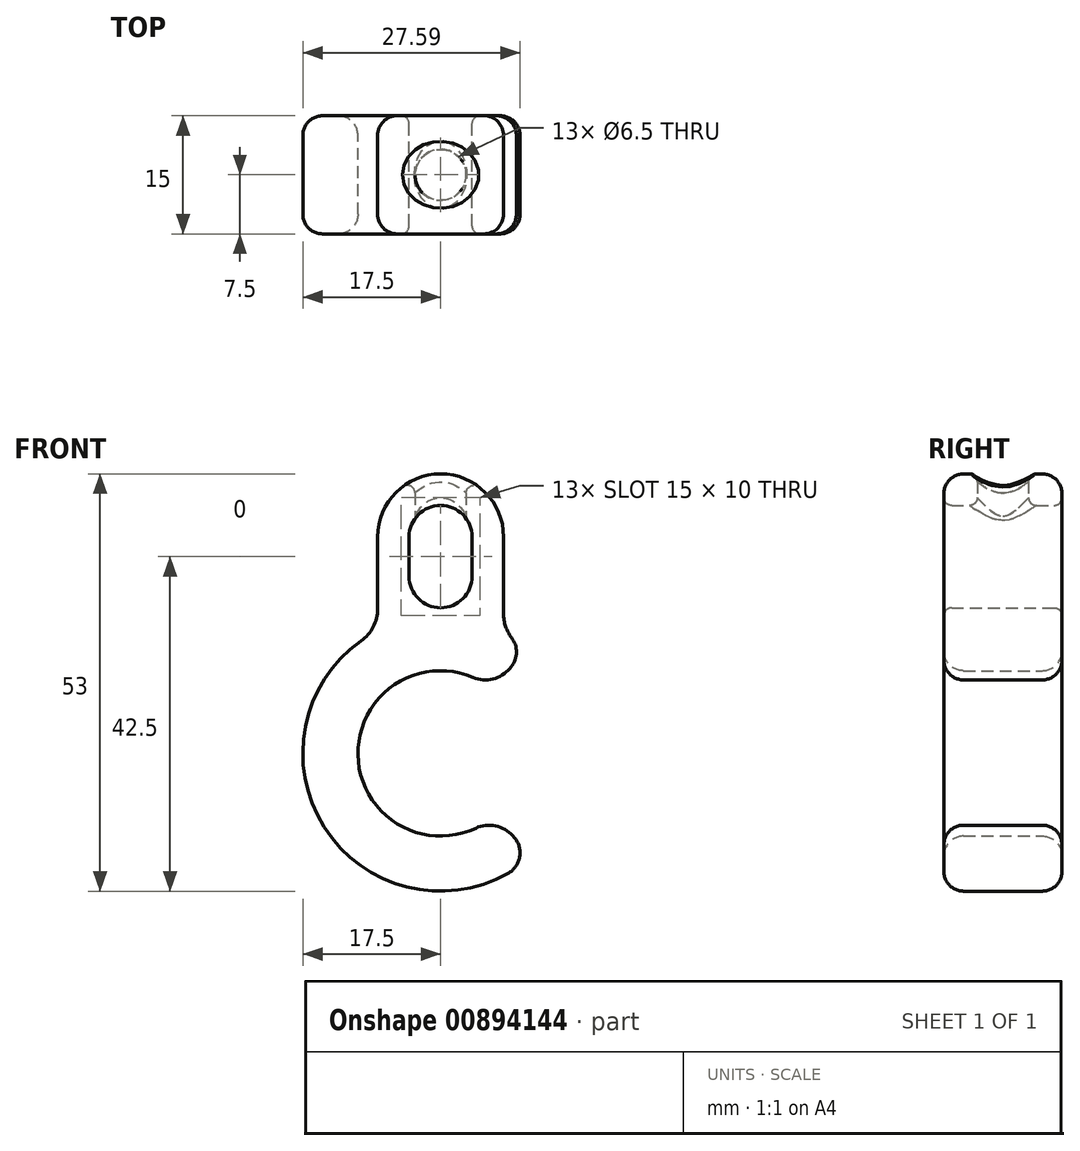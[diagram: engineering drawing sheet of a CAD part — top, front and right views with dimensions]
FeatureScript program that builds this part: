
annotation { "Feature Type Name" : "Feature", "Feature Type Description" : "" }
export const myFeature = defineFeature(function(context is Context, id is Id, definition is map)
    precondition{}
    {
        {
            var Q0;
            Q0=qCreatedBy(makeId("Front.planeOp"),FACE);
            var sketch = newSketch(context, id + "F0", { "sketchPlane" : qUnion([Q0])});
            skArc(sketch, "E0", {"start": v(4.12, 9.66) * mm, "mid": v(-10.5, -0.2) * mm, "end": v(4.47, -9.5) * mm});
            skLineSegment(sketch, "E1", {"start": v(8, 15.56) * mm, "end": v(8, 15.56) * mm});
            skLineSegment(sketch, "E2.left", {"start": v(-8, 15.56) * mm, "end": v(-8, 27.5) * mm});
            skLineSegment(sketch, "E2.right", {"start": v(8, 15.56) * mm, "end": v(8, 27.5) * mm});
            skPoint(sketch, "E2.middle", {"position": v(0, 21.53) * mm});
            skLineSegment(sketch, "E3", {"start": v(8.8, 10.8) * mm, "end": v(8.96, 11) * mm});
            skLineSegment(sketch, "E4", {"start": v(9.19, -10.48) * mm, "end": v(9.35, -10.67) * mm});
            skArc(sketch, "E5.trimOffspring", {"start": v(-8, 15.56) * mm, "mid": v(-15.42, -8.28) * mm, "end": v(8.56, -15.26) * mm});
            skLineSegment(sketch, "E6.left", {"start": v(4, 22.5) * mm, "end": v(4, 27.5) * mm});
            skLineSegment(sketch, "E6.right", {"start": v(-4, 22.5) * mm, "end": v(-4, 27.5) * mm});
            skPoint(sketch, "E6.middle", {"position": v(0, 25) * mm});
            skArc(sketch, "E7", {"start": v(4, 27.5) * mm, "mid": v(0, 31.5) * mm, "end": v(-4, 27.5) * mm});
            skArc(sketch, "E8", {"start": v(-4, 22.5) * mm, "mid": v(0, 18.5) * mm, "end": v(4, 22.5) * mm});
            skArc(sketch, "E9", {"start": v(8, 27.5) * mm, "mid": v(0, 35.5) * mm, "end": v(-8, 27.5) * mm});
            skPoint(sketch, "E10.visualSharp", {"position": v(6.63, 8.14) * mm});
            skArc(sketch, "E10.filletArc", {"start": v(4.12, 9.66) * mm, "mid": v(6.65, 9.45) * mm, "end": v(8.8, 10.8) * mm});
            skPoint(sketch, "E11.visualSharp", {"position": v(11.05, 13.57) * mm});
            skArc(sketch, "E11.filletArc", {"start": v(8.96, 11) * mm, "mid": v(9.56, 13.51) * mm, "end": v(8, 15.56) * mm});
            skPoint(sketch, "E12.visualSharp", {"position": v(6.92, -7.9) * mm});
            skArc(sketch, "E12.filletArc", {"start": v(9.19, -10.48) * mm, "mid": v(7, -9.2) * mm, "end": v(4.47, -9.5) * mm});
            skPoint(sketch, "E13.visualSharp", {"position": v(11.53, -13.16) * mm});
            skArc(sketch, "E13.filletArc", {"start": v(8.56, -15.26) * mm, "mid": v(10.05, -13.15) * mm, "end": v(9.35, -10.67) * mm});
            skSolve(sketch);
        }
        {
            var Q0;
            Q0 = qSketchRegion(id + "F0", true);
            extrude(context, id + "F1", {"entities" : qUnion([Q0]), "endBound" : BoundingType.SYMMETRIC, "depth" : 15 * mm, "offsetDistance" : 25 * mm});
        }
        {
            var Q0;
            Q0=qCreatedBy(makeId("Top.planeOp"),FACE);
            cPlane(context, id + "F2", {"entities" : qUnion([Q0]), "cplaneType" : CPlaneType.OFFSET, "offset" : 25 * mm, "width" : 150 * mm, "height" : 150 * mm});
        }
        {
            var Q0;
            Q0=qCreatedBy(id+"F2.planeOp",FACE);
            var sketch = newSketch(context, id + "F3", { "sketchPlane" : qUnion([Q0])});
            skCircle(sketch, "E14", {"center": v(0, 0) * mm, "radius": 3.25 * mm});
            skSolve(sketch);
        }
        {
            var Q0;
            Q0 = qSketchRegion(id + "F3", true);
            extrude(context, id + "F4", {"entities" : qUnion([Q0]), "operationType" : NewBodyOperationType.REMOVE, "depth" : 25 * mm, "offsetDistance" : 25 * mm});
        }
        {
            var Q0;
            {var subQ0=sQuery(id+"F0.wireOp",EDGE,"E8");Q0=makeQuery(id+"F6.opFillet","BLEND_EDGE",EDGE,{"blendedFrom":[makeQuery(id+"F1.opExtrude","CAP_EDGE",EDGE,{"disambiguationData":[OSD([subQ0])],"isStart":false}),makeQuery(id+"F1.opExtrude","CAP_FACE",FACE,{"disambiguationData":[OSD([sQuery(id+"F0.wireOp",EDGE,"E0"),sQuery(id+"F0.wireOp",EDGE,"E1"),sQuery(id+"F0.wireOp",EDGE,"E2.left"),sQuery(id+"F0.wireOp",EDGE,"E2.right"),sQuery(id+"F0.wireOp",EDGE,"E3"),sQuery(id+"F0.wireOp",EDGE,"E4"),sQuery(id+"F0.wireOp",EDGE,"E5.trimOffspring"),sQuery(id+"F0.wireOp",EDGE,"E6.left"),sQuery(id+"F0.wireOp",EDGE,"E6.right"),sQuery(id+"F0.wireOp",EDGE,"E7"),subQ0,sQuery(id+"F0.wireOp",EDGE,"E9"),sQuery(id+"F0.wireOp",EDGE,"E10.filletArc"),sQuery(id+"F0.wireOp",EDGE,"E11.filletArc"),sQuery(id+"F0.wireOp",EDGE,"E12.filletArc"),sQuery(id+"F0.wireOp",EDGE,"E13.filletArc")])],"isStart":false})],"blendedInto":[makeQuery(id+"F1.opExtrude","CAP_FACE",FACE,{"disambiguationData":[OSD([sQuery(id+"F0.wireOp",EDGE,"E0"),sQuery(id+"F0.wireOp",EDGE,"E1"),sQuery(id+"F0.wireOp",EDGE,"E2.left"),sQuery(id+"F0.wireOp",EDGE,"E2.right"),sQuery(id+"F0.wireOp",EDGE,"E3"),sQuery(id+"F0.wireOp",EDGE,"E4"),sQuery(id+"F0.wireOp",EDGE,"E5.trimOffspring"),sQuery(id+"F0.wireOp",EDGE,"E6.left"),sQuery(id+"F0.wireOp",EDGE,"E6.right"),sQuery(id+"F0.wireOp",EDGE,"E7"),subQ0,sQuery(id+"F0.wireOp",EDGE,"E9"),sQuery(id+"F0.wireOp",EDGE,"E10.filletArc"),sQuery(id+"F0.wireOp",EDGE,"E11.filletArc"),sQuery(id+"F0.wireOp",EDGE,"E12.filletArc"),sQuery(id+"F0.wireOp",EDGE,"E13.filletArc")])],"isStart":false})]});}
            var Q1;
            Q1=makeQuery(id+"F1.opExtrude","SWEPT_EDGE",EDGE,{"disambiguationData":[OSD([sQuery(id+"F0.wireOp",EDGE,"E2.left"),sQuery(id+"F0.wireOp",EDGE,"E5.trimOffspring")])]});
            var Q2;
            Q2=makeQuery(id+"F1.opExtrude","SWEPT_EDGE",EDGE,{"disambiguationData":[OSD([sQuery(id+"F0.wireOp",EDGE,"E1"),sQuery(id+"F0.wireOp",EDGE,"E2.right")])]});
            fillet(context, id + "F5", {"entities" : qUnion([Q0, Q1, Q2]), "radius" : 5 * mm, "tangentPropagation" : true, "allowEdgeOverflow" : false});
        }
        {
            var Q0;
            Q0=makeQuery(id+"F1.opExtrude","CAP_EDGE",EDGE,{"disambiguationData":[OSD([sQuery(id+"F0.wireOp",EDGE,"E2.left")])],"isStart":false});
            var Q1;
            Q1=makeQuery(id+"F1.opExtrude","CAP_EDGE",EDGE,{"disambiguationData":[OSD([sQuery(id+"F0.wireOp",EDGE,"E2.left")])],"isStart":true});
            fillet(context, id + "F6", {"entities" : qUnion([Q0, Q1]), "radius" : 2.5 * mm, "tangentPropagation" : true, "allowEdgeOverflow" : false});
        }
        {
            var Q0;
            Q0=makeQuery(id+"F4.boolean.opBoolean","COPY",FACE,{"derivedFrom":makeQuery(id+"F4.opExtrude","SWEPT_FACE",FACE,{"disambiguationData":[OSD([sQuery(id+"F3.wireOp",EDGE,"E14")])]})});
            var Q1;
            Q1=makeQuery(id+"F1.opExtrude","CAP_EDGE",EDGE,{"disambiguationData":[OSD([sQuery(id+"F0.wireOp",EDGE,"E6.right")])],"isStart":false});
            var Q2;
            Q2=makeQuery(id+"F1.opExtrude","CAP_EDGE",EDGE,{"disambiguationData":[OSD([sQuery(id+"F0.wireOp",EDGE,"E6.right")])],"isStart":true});
            fillet(context, id + "F7", {"entities" : qUnion([Q0, Q1, Q2]), "radius" : 1 * mm, "tangentPropagation" : true, "allowEdgeOverflow" : false});
        }
    });
